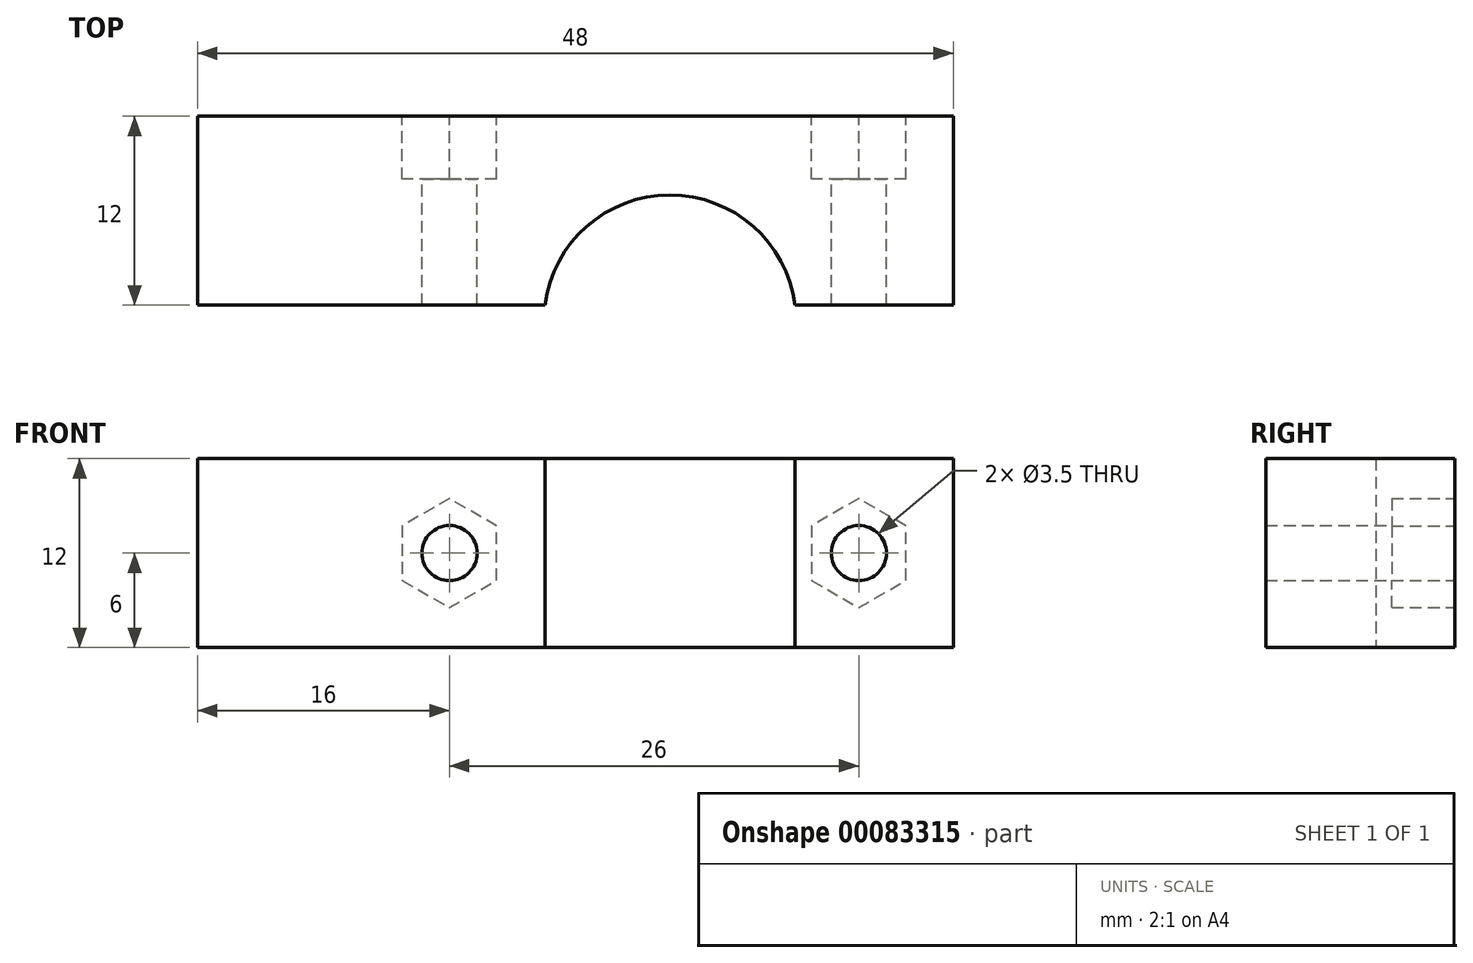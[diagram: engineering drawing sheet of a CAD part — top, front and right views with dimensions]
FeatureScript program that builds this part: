
annotation { "Feature Type Name" : "Feature", "Feature Type Description" : "" }
export const myFeature = defineFeature(function(context is Context, id is Id, definition is map)
    precondition{}
    {
        {
            var Q0;
            Q0=qCreatedBy(makeId("Top.planeOp"),FACE);
            var sketch = newSketch(context, id + "F0", { "sketchPlane" : qUnion([Q0])});
            skLineSegment(sketch, "E0.bottom", {"start": v(0, 0) * mm, "end": v(22.06, 0) * mm});
            skLineSegment(sketch, "E0.top", {"start": v(0, 12) * mm, "end": v(48, 12) * mm});
            skLineSegment(sketch, "E0.left", {"start": v(0, 0) * mm, "end": v(0, 12) * mm});
            skLineSegment(sketch, "E0.right", {"start": v(48, 0) * mm, "end": v(48, 12) * mm});
            skArc(sketch, "E1", {"start": v(37.94, 0) * mm, "mid": v(30, 7) * mm, "end": v(22.06, 0) * mm});
            skLineSegment(sketch, "E2.trimOffspring", {"start": v(37.94, 0) * mm, "end": v(48, 0) * mm});
            skSolve(sketch);
        }
        {
            var Q0;
            Q0 = qSketchRegion(id + "F0", true);
            extrude(context, id + "F1", {"entities" : qUnion([Q0]), "depth" : 12 * mm, "offsetDistance" : 25 * mm});
        }
        {
            var Q0;
            Q0=makeQuery(id+"F1.opExtrude","SWEPT_FACE",FACE,{"disambiguationData":[OSD([sQuery(id+"F0.wireOp",EDGE,"E0.top")])]});
            var sketch = newSketch(context, id + "F2", { "sketchPlane" : qUnion([Q0])});
            skCircle(sketch, "E3", {"center": v(-42, 6) * mm, "radius": 1.75 * mm});
            skCircle(sketch, "E4", {"center": v(-16, 6) * mm, "radius": 1.75 * mm});
            skCircle(sketch, "E5.cCircle", {"center": v(-42, 6) * mm, "radius": 3 * mm, "construction": true});
            skLineSegment(sketch, "E5.0", {"start": v(-39, 7.73) * mm, "end": v(-39, 4.27) * mm});
            skLineSegment(sketch, "E5.1", {"start": v(-39, 4.27) * mm, "end": v(-42, 2.54) * mm});
            skLineSegment(sketch, "E5.2", {"start": v(-42, 2.54) * mm, "end": v(-45, 4.27) * mm});
            skLineSegment(sketch, "E5.3", {"start": v(-45, 4.27) * mm, "end": v(-45, 7.73) * mm});
            skLineSegment(sketch, "E5.4", {"start": v(-45, 7.73) * mm, "end": v(-42, 9.46) * mm});
            skLineSegment(sketch, "E5.5", {"start": v(-42, 9.46) * mm, "end": v(-39, 7.73) * mm});
            skPoint(sketch, "E5.0.midPoint", {"position": v(-39, 6) * mm});
            skCircle(sketch, "E6.cCircle", {"center": v(-16, 6) * mm, "radius": 3 * mm, "construction": true});
            skLineSegment(sketch, "E6.0", {"start": v(-16, 9.46) * mm, "end": v(-13, 7.73) * mm});
            skLineSegment(sketch, "E6.1", {"start": v(-13, 7.73) * mm, "end": v(-13, 4.27) * mm});
            skLineSegment(sketch, "E6.2", {"start": v(-13, 4.27) * mm, "end": v(-16, 2.54) * mm});
            skLineSegment(sketch, "E6.3", {"start": v(-16, 2.54) * mm, "end": v(-19, 4.27) * mm});
            skLineSegment(sketch, "E6.4", {"start": v(-19, 4.27) * mm, "end": v(-19, 7.73) * mm});
            skLineSegment(sketch, "E6.5", {"start": v(-19, 7.73) * mm, "end": v(-16, 9.46) * mm});
            skPoint(sketch, "E6.0.midPoint", {"position": v(-14.5, 8.6) * mm});
            skSolve(sketch);
        }
        {
            var Q0;
            Q0=makeQuery(id+"F2.imprint","IMPRINT",FACE,{"disambiguationData":[TD([[makeQuery(id+"F2.imprint","IMPRINT",EDGE,{"derivedFrom":sQuery(id+"F2.wireOp",EDGE,"E3")}),1.0]])]});
            var Q1;
            Q1=makeQuery(id+"F2.imprint","IMPRINT",FACE,{"disambiguationData":[TD([[makeQuery(id+"F2.imprint","IMPRINT",EDGE,{"derivedFrom":sQuery(id+"F2.wireOp",EDGE,"E4")}),1.0]])]});
            extrude(context, id + "F3", {"entities" : qUnion([Q0, Q1]), "operationType" : NewBodyOperationType.REMOVE, "endBound" : BoundingType.UP_TO_NEXT, "oppositeDirection" : true, "depth" : 25 * mm, "offsetDistance" : 25 * mm});
        }
        {
            var Q0;
            Q0=makeQuery(id+"F2.imprint","IMPRINT",FACE,{"disambiguationData":[TD([[makeQuery(id+"F2.imprint","IMPRINT",EDGE,{"derivedFrom":sQuery(id+"F2.wireOp",EDGE,"E3")}),-1.0]])]});
            var Q1;
            Q1=makeQuery(id+"F2.imprint","IMPRINT",FACE,{"disambiguationData":[TD([[makeQuery(id+"F2.imprint","IMPRINT",EDGE,{"derivedFrom":sQuery(id+"F2.wireOp",EDGE,"E4")}),-1.0]])]});
            extrude(context, id + "F4", {"entities" : qUnion([Q0, Q1]), "operationType" : NewBodyOperationType.REMOVE, "oppositeDirection" : true, "depth" : 4 * mm, "offsetDistance" : 25 * mm});
        }
    });
